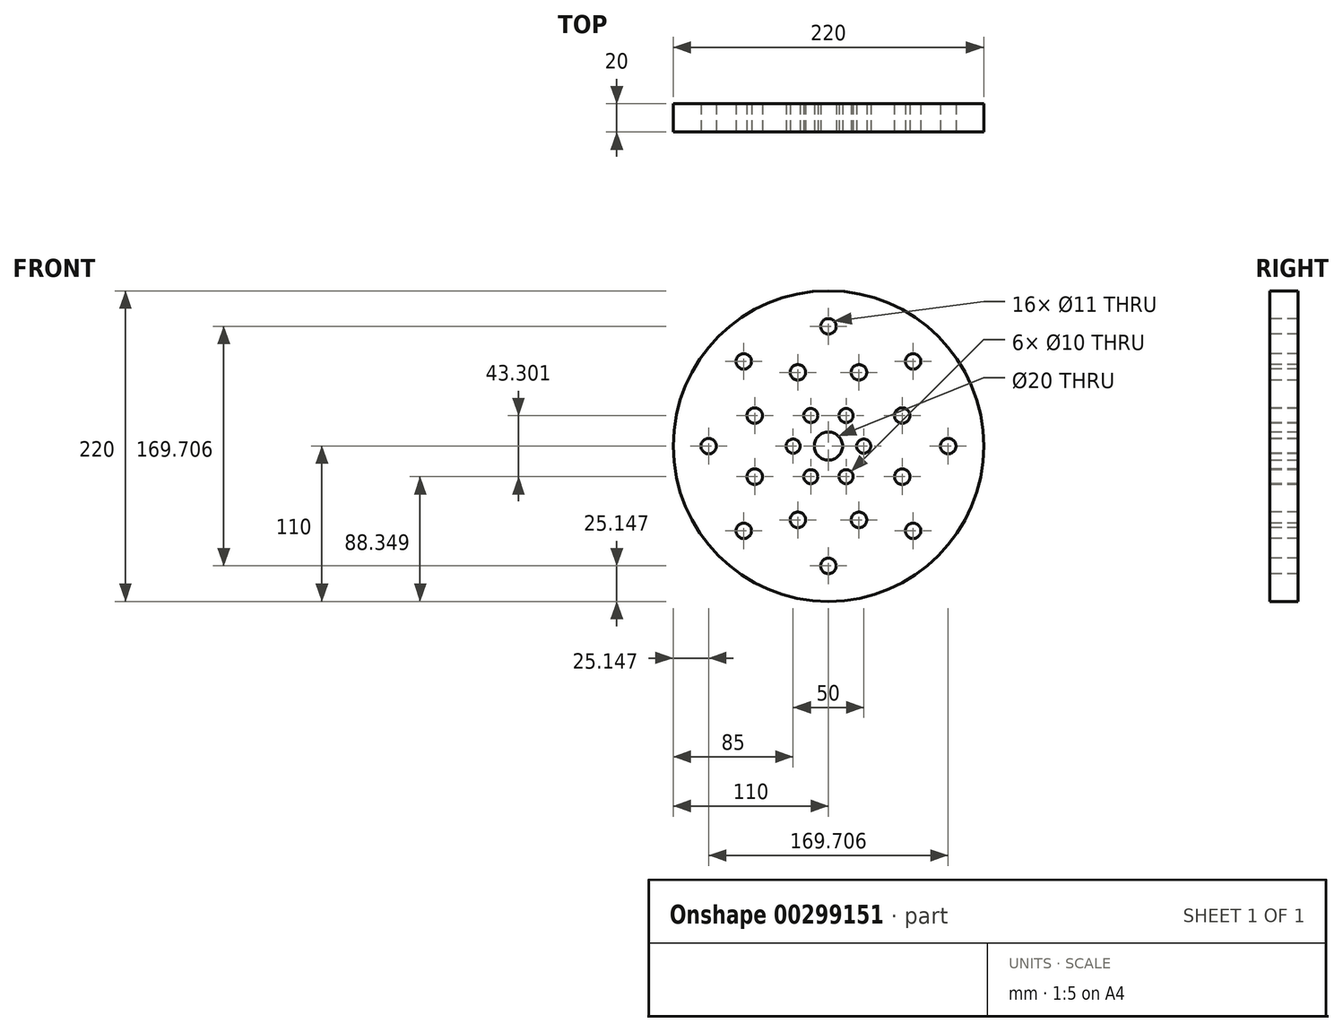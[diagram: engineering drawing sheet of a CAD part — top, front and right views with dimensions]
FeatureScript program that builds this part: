
annotation { "Feature Type Name" : "Feature", "Feature Type Description" : "" }
export const myFeature = defineFeature(function(context is Context, id is Id, definition is map)
    precondition{}
    {
        {
            var Q0;
            Q0=qCreatedBy(makeId("Front.planeOp"),FACE);
            var sketch = newSketch(context, id + "F0", { "sketchPlane" : qUnion([Q0])});
            skCircle(sketch, "E0", {"center": v(0, 0) * mm, "radius": 110 * mm});
            skSolve(sketch);
        }
        {
            var Q0;
            Q0 = qSketchRegion(id + "F0", true);
            extrude(context, id + "F1", {"entities" : qUnion([Q0]), "depth" : 20 * mm});
        }
        {
            var Q0;
            Q0=makeQuery(id+"F1.opExtrude","CAP_FACE",FACE,{"disambiguationData":[OSD([sQuery(id+"F0.wireOp",EDGE,"E0")])],"isStart":false});
            var sketch = newSketch(context, id + "F2", { "sketchPlane" : qUnion([Q0])});
            skCircle(sketch, "E1", {"center": v(84.85, 0) * mm, "radius": 5.5 * mm});
            skCircle(sketch, "E2.1.0", {"center": v(60, 60) * mm, "radius": 5.5 * mm});
            skCircle(sketch, "E2.2.0", {"center": v(0, 84.85) * mm, "radius": 5.5 * mm});
            skCircle(sketch, "E2.3.0", {"center": v(-60, 60) * mm, "radius": 5.5 * mm});
            skCircle(sketch, "E2.4.0", {"center": v(-84.85, 0) * mm, "radius": 5.5 * mm});
            skCircle(sketch, "E2.5.0", {"center": v(-60, -60) * mm, "radius": 5.5 * mm});
            skCircle(sketch, "E2.6.0", {"center": v(0, -84.85) * mm, "radius": 5.5 * mm});
            skCircle(sketch, "E2.7.0", {"center": v(60, -60) * mm, "radius": 5.5 * mm});
            skPoint(sketch, "E2.center", {"position": v(0, 0) * mm});
            skCircle(sketch, "E3", {"center": v(0, 0) * mm, "radius": 10 * mm});
            skCircle(sketch, "E4", {"center": v(52.26, 21.65) * mm, "radius": 5.5 * mm});
            skCircle(sketch, "E5.1.0", {"center": v(52.26, -21.65) * mm, "radius": 5.5 * mm});
            skCircle(sketch, "E5.2.0", {"center": v(21.65, -52.26) * mm, "radius": 5.5 * mm});
            skCircle(sketch, "E5.3.0", {"center": v(-21.65, -52.26) * mm, "radius": 5.5 * mm});
            skCircle(sketch, "E5.4.0", {"center": v(-52.26, -21.65) * mm, "radius": 5.5 * mm});
            skCircle(sketch, "E5.5.0", {"center": v(-52.26, 21.65) * mm, "radius": 5.5 * mm});
            skCircle(sketch, "E5.6.0", {"center": v(-21.65, 52.26) * mm, "radius": 5.5 * mm});
            skCircle(sketch, "E5.7.0", {"center": v(21.65, 52.26) * mm, "radius": 5.5 * mm});
            skLineSegment(sketch, "E5.anchor1", {"start": v(0, 0) * mm, "end": v(52.26, 21.65) * mm, "construction": true});
            skLineSegment(sketch, "E5.anchor2", {"start": v(0, 0) * mm, "end": v(21.65, 52.26) * mm, "construction": true});
            skSolve(sketch);
        }
        {
            var Q0;
            Q0 = qSketchRegion(id + "F2", true);
            extrude(context, id + "F3", {"entities" : qUnion([Q0]), "operationType" : NewBodyOperationType.REMOVE, "oppositeDirection" : true, "depth" : 25 * mm});
        }
        {
            var Q0;
            Q0=makeQuery(id+"F1.opExtrude","CAP_FACE",FACE,{"disambiguationData":[OSD([sQuery(id+"F0.wireOp",EDGE,"E0")])],"isStart":false});
            var sketch = newSketch(context, id + "F4", { "sketchPlane" : qUnion([Q0])});
            skCircle(sketch, "E6", {"center": v(25, 0) * mm, "radius": 5 * mm});
            skCircle(sketch, "E7.1.0", {"center": v(12.5, 21.65) * mm, "radius": 5 * mm});
            skCircle(sketch, "E7.2.0", {"center": v(-12.5, 21.65) * mm, "radius": 5 * mm});
            skCircle(sketch, "E7.3.0", {"center": v(-25, 0) * mm, "radius": 5 * mm});
            skCircle(sketch, "E7.4.0", {"center": v(-12.5, -21.65) * mm, "radius": 5 * mm});
            skCircle(sketch, "E7.5.0", {"center": v(12.5, -21.65) * mm, "radius": 5 * mm});
            skPoint(sketch, "E7.center", {"position": v(0, 0) * mm});
            skSolve(sketch);
        }
        {
            var Q0;
            Q0 = qSketchRegion(id + "F4", true);
            extrude(context, id + "F5", {"entities" : qUnion([Q0]), "operationType" : NewBodyOperationType.REMOVE, "oppositeDirection" : true, "depth" : 25 * mm});
        }
    });
